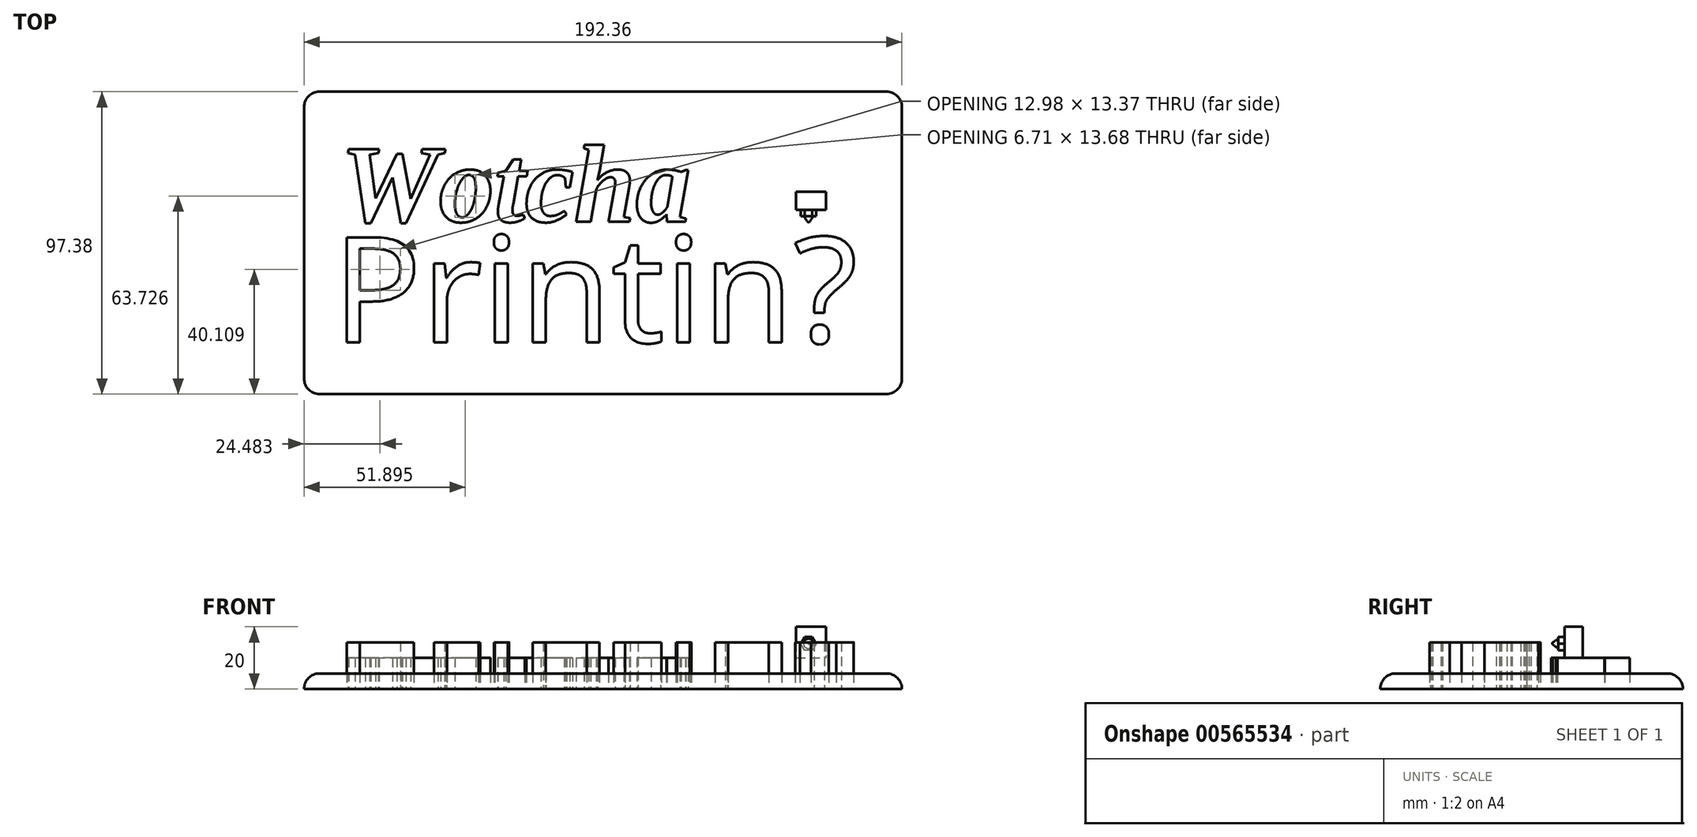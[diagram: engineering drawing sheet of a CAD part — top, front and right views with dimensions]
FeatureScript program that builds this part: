
annotation { "Feature Type Name" : "Feature", "Feature Type Description" : "" }
export const myFeature = defineFeature(function(context is Context, id is Id, definition is map)
    precondition{}
    {
        {
            var Q0;
            Q0=qCreatedBy(makeId("Top.planeOp"),FACE);
            var sketch = newSketch(context, id + "F0", { "sketchPlane" : qUnion([Q0])});
            skText(sketch, "E0", { "text": "Wotcha", "fontName": "Tinos-BoldItalic.ttf"});
            const initialGuessF0  = {"E0": [-0.04924, 0.01918, 1, 0, 0.02564]};
            skSetInitialGuess(sketch, initialGuessF0);
            skSolve(sketch);
        }
        {
            var Q0;
            Q0 = qSketchRegion(id + "F0", true);
            extrude(context, id + "F1", {"entities" : qUnion([Q0]), "depth" : 10 * mm, "offsetDistance" : 25 * mm});
        }
        {
            var Q0;
            Q0=qCreatedBy(makeId("Top.planeOp"),FACE);
            var sketch = newSketch(context, id + "F2", { "sketchPlane" : qUnion([Q0])});
            skText(sketch, "E1", { "text": "Printin?", "fontName": "NotoSans-Regular.ttf"});
            const initialGuessF2  = {"E1": [-0.05182, -0.01973, 1, 0, 0.03412]};
            skSetInitialGuess(sketch, initialGuessF2);
            skSolve(sketch);
        }
        {
            var Q0;
            Q0 = qSketchRegion(id + "F2", true);
            extrude(context, id + "F3", {"entities" : qUnion([Q0]), "depth" : 15 * mm, "offsetDistance" : 25 * mm});
        }
        {
            var Q0;
            Q0=qCreatedBy(makeId("Top.planeOp"),FACE);
            var sketch = newSketch(context, id + "F4", { "sketchPlane" : qUnion([Q0])});
            skLineSegment(sketch, "E2.bottom", {"start": v(-55.95, 61.05) * mm, "end": v(126.41, 61.05) * mm});
            skLineSegment(sketch, "E2.top", {"start": v(-55.95, -36.33) * mm, "end": v(126.41, -36.33) * mm});
            skLineSegment(sketch, "E2.left", {"start": v(-60.95, 56.05) * mm, "end": v(-60.95, -31.33) * mm});
            skLineSegment(sketch, "E2.right", {"start": v(131.41, 56.05) * mm, "end": v(131.41, -31.33) * mm});
            skPoint(sketch, "E3.visualSharp", {"position": v(-60.95, 61.05) * mm});
            skArc(sketch, "E3.filletArc", {"start": v(-55.95, 61.05) * mm, "mid": v(-59.48, 59.58) * mm, "end": v(-60.95, 56.05) * mm});
            skPoint(sketch, "E4.visualSharp", {"position": v(131.41, 61.05) * mm});
            skArc(sketch, "E4.filletArc", {"start": v(131.41, 56.05) * mm, "mid": v(129.95, 59.58) * mm, "end": v(126.41, 61.05) * mm});
            skPoint(sketch, "E5.visualSharp", {"position": v(131.41, -36.33) * mm});
            skArc(sketch, "E5.filletArc", {"start": v(126.41, -36.33) * mm, "mid": v(129.95, -34.87) * mm, "end": v(131.41, -31.33) * mm});
            skPoint(sketch, "E6.visualSharp", {"position": v(-60.95, -36.33) * mm});
            skArc(sketch, "E6.filletArc", {"start": v(-60.95, -31.33) * mm, "mid": v(-59.48, -34.87) * mm, "end": v(-55.95, -36.33) * mm});
            skSolve(sketch);
        }
        {
            var Q0;
            Q0=makeQuery(id+"F4.imprint","IMPRINT",FACE,{"disambiguationData":[TD([[makeQuery(id+"F4.imprint","IMPRINT",EDGE,{"derivedFrom":sQuery(id+"F4.wireOp",EDGE,"E2.bottom")}),-1.0]])]});
            extrude(context, id + "F5", {"entities" : qUnion([Q0]), "depth" : 5 * mm, "offsetDistance" : 25 * mm});
        }
        {
            var Q0;
            Q0=makeQuery(id+"F5.opExtrude","CAP_EDGE",EDGE,{"disambiguationData":[OSD([sQuery(id+"F4.wireOp",EDGE,"E2.bottom")])],"isStart":false});
            fillet(context, id + "F6", {"entities" : qUnion([Q0]), "radius" : 5 * mm, "tangentPropagation" : true, "allowEdgeOverflow" : false});
        }
        {
            var Q0;
            Q0=makeQuery(id+"F5.opExtrude","CAP_FACE",FACE,{"disambiguationData":[OSD([sQuery(id+"F4.wireOp",EDGE,"E2.bottom"),sQuery(id+"F4.wireOp",EDGE,"E2.top"),sQuery(id+"F4.wireOp",EDGE,"E2.left"),sQuery(id+"F4.wireOp",EDGE,"E2.right"),sQuery(id+"F4.wireOp",EDGE,"E3.filletArc"),sQuery(id+"F4.wireOp",EDGE,"E4.filletArc"),sQuery(id+"F4.wireOp",EDGE,"E5.filletArc"),sQuery(id+"F4.wireOp",EDGE,"E6.filletArc")])],"isStart":false});
            cPlane(context, id + "F7", {"entities" : qUnion([Q0]), "cplaneType" : CPlaneType.OFFSET, "offset" : 5 * mm, "width" : 150 * mm, "height" : 150 * mm});
        }
        {
            var Q0;
            Q0=qCreatedBy(id+"F7.planeOp",FACE);
            var sketch = newSketch(context, id + "F8", { "sketchPlane" : qUnion([Q0])});
            skLineSegment(sketch, "E7.bottom", {"start": v(97.34, 28.77) * mm, "end": v(106.93, 28.77) * mm});
            skLineSegment(sketch, "E7.top", {"start": v(97.34, 22.99) * mm, "end": v(106.93, 22.99) * mm});
            skLineSegment(sketch, "E7.left", {"start": v(97.34, 28.77) * mm, "end": v(97.34, 22.99) * mm});
            skLineSegment(sketch, "E7.right", {"start": v(106.93, 28.77) * mm, "end": v(106.93, 22.99) * mm});
            skSolve(sketch);
        }
        {
            var Q0;
            Q0 = qSketchRegion(id + "F8", true);
            extrude(context, id + "F9", {"entities" : qUnion([Q0]), "depth" : 10 * mm, "offsetDistance" : 25 * mm});
        }
        {
            var Q0;
            Q0=makeQuery(id+"F9.opExtrude","SWEPT_FACE",FACE,{"disambiguationData":[OSD([sQuery(id+"F8.wireOp",EDGE,"E7.top")])]});
            var sketch = newSketch(context, id + "F10", { "sketchPlane" : qUnion([Q0])});
            skLineSegment(sketch, "E8", {"start": v(100.14, 16.73) * mm, "end": v(102.6, 16.73) * mm});
            skLineSegment(sketch, "E9", {"start": v(102.6, 16.73) * mm, "end": v(103.82, 14.6) * mm});
            skLineSegment(sketch, "E10", {"start": v(103.82, 14.6) * mm, "end": v(102.6, 12.48) * mm});
            skLineSegment(sketch, "E11", {"start": v(102.6, 12.48) * mm, "end": v(100.14, 12.48) * mm});
            skLineSegment(sketch, "E12", {"start": v(100.14, 12.48) * mm, "end": v(98.9, 14.6) * mm});
            skLineSegment(sketch, "E13", {"start": v(98.9, 14.6) * mm, "end": v(100.14, 16.73) * mm});
            skSolve(sketch);
        }
        {
            var Q0;
            Q0=makeQuery(id+"F10.imprint","IMPRINT",FACE,{"disambiguationData":[TD([[makeQuery(id+"F10.imprint","IMPRINT",EDGE,{"derivedFrom":sQuery(id+"F10.wireOp",EDGE,"E8")}),-1.0]])]});
            extrude(context, id + "F11", {"entities" : qUnion([Q0]), "operationType" : NewBodyOperationType.ADD, "depth" : 2 * mm, "offsetDistance" : 25 * mm});
        }
        {
            var Q0;
            Q0=makeQuery(id+"F11.opExtrude","CAP_FACE",FACE,{"disambiguationData":[OSD([sQuery(id+"F10.wireOp",EDGE,"E8"),sQuery(id+"F10.wireOp",EDGE,"E9"),sQuery(id+"F10.wireOp",EDGE,"E10"),sQuery(id+"F10.wireOp",EDGE,"E11"),sQuery(id+"F10.wireOp",EDGE,"E12"),sQuery(id+"F10.wireOp",EDGE,"E13")])],"isStart":false});
            cPlane(context, id + "F12", {"entities" : qUnion([Q0]), "cplaneType" : CPlaneType.OFFSET, "offset" : 2 * mm, "width" : 150 * mm, "height" : 150 * mm});
        }
        {
            var Q0;
            Q0=makeQuery(id+"F11.opExtrude","CAP_FACE",FACE,{"disambiguationData":[OSD([sQuery(id+"F10.wireOp",EDGE,"E8"),sQuery(id+"F10.wireOp",EDGE,"E9"),sQuery(id+"F10.wireOp",EDGE,"E10"),sQuery(id+"F10.wireOp",EDGE,"E11"),sQuery(id+"F10.wireOp",EDGE,"E12"),sQuery(id+"F10.wireOp",EDGE,"E13")])],"isStart":false});
            var sketch = newSketch(context, id + "F13", { "sketchPlane" : qUnion([Q0])});
            skCircle(sketch, "E14", {"center": v(101.36, 14.6) * mm, "radius": 1.59 * mm});
            skSolve(sketch);
        }
        {
            var Q0;
            Q0=qCreatedBy(id+"F12.planeOp",FACE);
            var sketch = newSketch(context, id + "F14", { "sketchPlane" : qUnion([Q0])});
            skCircle(sketch, "E15", {"center": v(101.4, 14.64) * mm, "radius": 0.23 * mm});
            skSolve(sketch);
        }
        {
            var Q1;
            Q1=makeQuery(id+"F13.imprint","IMPRINT",FACE,{"disambiguationData":[TD([[makeQuery(id+"F13.imprint","IMPRINT",EDGE,{"derivedFrom":sQuery(id+"F13.wireOp",EDGE,"E14")}),1.0]])]});
            var Q2;
            Q2=makeQuery(id+"F14.imprint","IMPRINT",FACE,{"disambiguationData":[TD([[makeQuery(id+"F14.imprint","IMPRINT",EDGE,{"derivedFrom":sQuery(id+"F14.wireOp",EDGE,"E15")}),1.0]])]});
            loft(context, id + "F15", {"operationType" : NewBodyOperationType.ADD, "sheetProfilesArray" : [{ "sheetProfileEntities" : qUnion([Q1]) }, { "sheetProfileEntities" : qUnion([Q2]) }]});
        }
    });
